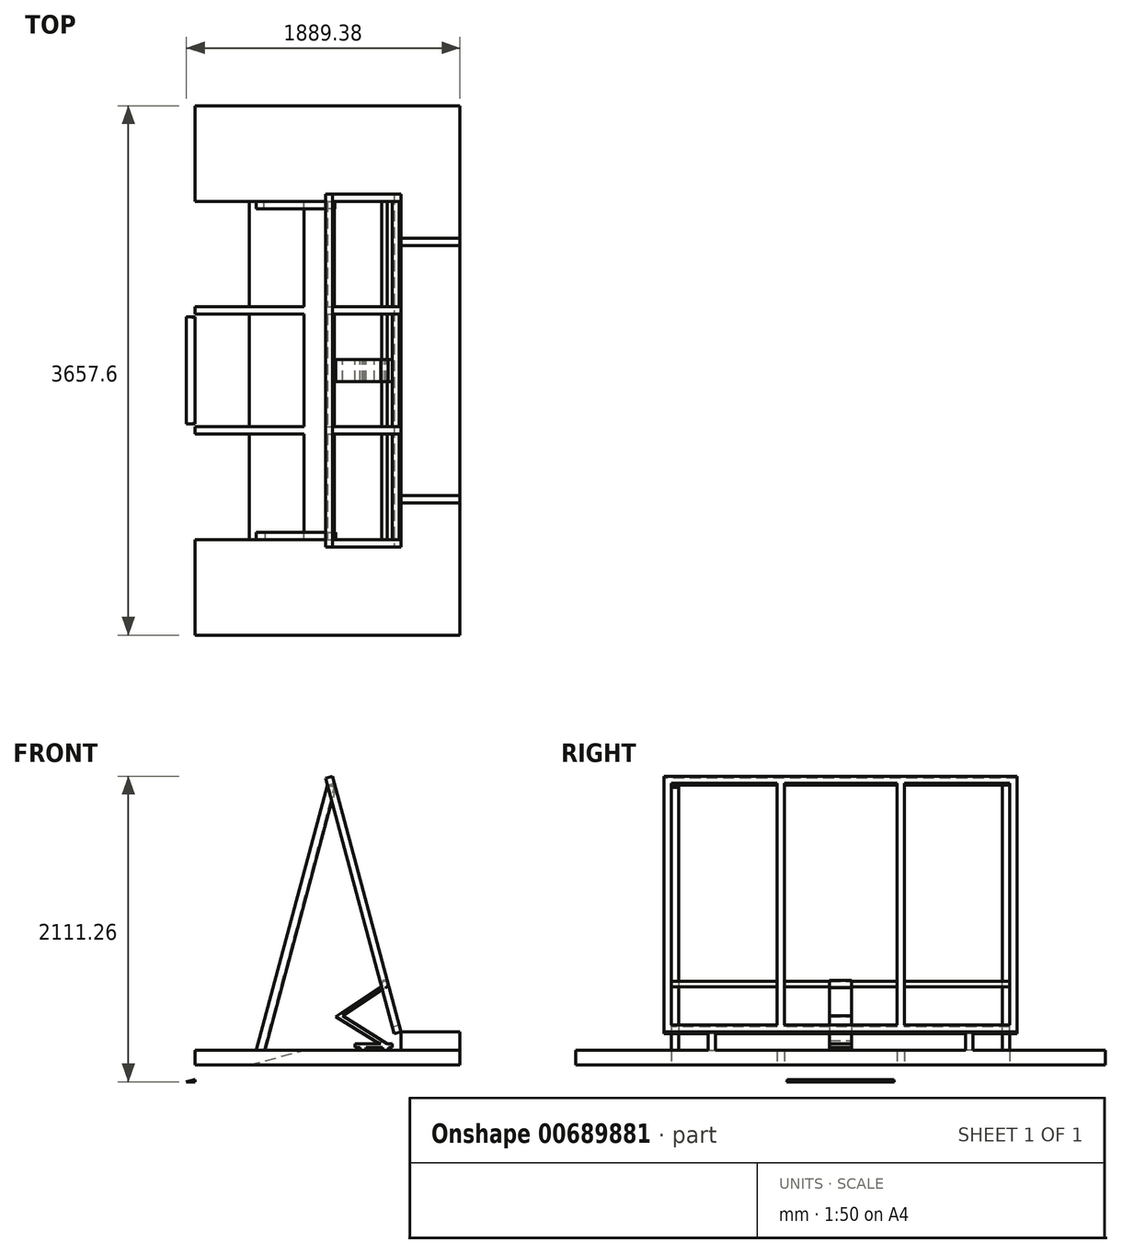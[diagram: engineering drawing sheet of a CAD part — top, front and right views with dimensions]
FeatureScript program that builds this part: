
annotation { "Feature Type Name" : "Feature", "Feature Type Description" : "" }
export const myFeature = defineFeature(function(context is Context, id is Id, definition is map)
    precondition{}
    {
        {
            var Q0;
            Q0=qCreatedBy(makeId("Top.planeOp"),FACE);
            var sketch = newSketch(context, id + "F0", { "sketchPlane" : qUnion([Q0])});
            skLineSegment(sketch, "E0.bottom", {"start": v(0, 0) * mm, "end": v(1828.8, 0) * mm});
            skLineSegment(sketch, "E0.top", {"start": v(0, 3657.6) * mm, "end": v(1828.8, 3657.6) * mm});
            skLineSegment(sketch, "E0.left", {"start": v(0, 0) * mm, "end": v(0, 3657.6) * mm});
            skLineSegment(sketch, "E0.right", {"start": v(1828.8, 0) * mm, "end": v(1828.8, 3657.6) * mm});
            skSolve(sketch);
        }
        {
            var Q0;
            Q0 = qSketchRegion(id + "F0", true);
            extrude(context, id + "F1", {"entities" : qUnion([Q0]), "oppositeDirection" : true, "depth" : 101.6 * mm, "offsetDistance" : 25.4 * mm});
        }
        {
            var Q0;
            Q0=qCreatedBy(makeId("Right.planeOp"),FACE);
            var sketch = newSketch(context, id + "F2", { "sketchPlane" : qUnion([Q0])});
            skArc(sketch, "E1", {"start": v(2199.73, -217.77) * mm, "mid": v(1828.8, 76.2) * mm, "end": v(1457.87, -217.77) * mm});
            skLineSegment(sketch, "E2", {"start": v(1457.87, -217.77) * mm, "end": v(2199.73, -217.77) * mm});
            skLineSegment(sketch, "E3", {"start": v(1657.07, 76.2) * mm, "end": v(2046.06, 76.2) * mm, "construction": true});
            skPoint(sketch, "E3.startSnap0", {"position": v(1828.8, 76.2) * mm});
            skSolve(sketch);
        }
        {
            var Q0;
            Q0 = qSketchRegion(id + "F2", true);
            extrude(context, id + "F3", {"entities" : qUnion([Q0]), "operationType" : NewBodyOperationType.ADD, "oppositeDirection" : true, "depth" : 304.8 * mm, "offsetDistance" : 25.4 * mm});
        }
        {
            var Q0;
            {var subQ0=sQuery(id+"F0.wireOp",EDGE,"E0.left");var subQ1=sQuery(id+"F2.wireOp",EDGE,"E1");Q0=makeQuery(id+"F3.boolean.opBoolean","SPLIT",FACE,{"disambiguationData":[TD([makeQuery(id+"F1.opExtrude","CAP_FACE",FACE,{"disambiguationData":[OSD([sQuery(id+"F0.wireOp",EDGE,"E0.bottom"),sQuery(id+"F0.wireOp",EDGE,"E0.top"),subQ0,sQuery(id+"F0.wireOp",EDGE,"E0.right")])],"isStart":true})])],"derivedFrom":makeQuery(id+"F3.opExtrude","CAP_FACE",FACE,{"disambiguationData":[OSD([subQ1,sQuery(id+"F2.wireOp",EDGE,"E2")])],"isStart":true})});}
            cPlane(context, id + "F4", {"entities" : qUnion([Q0]), "cplaneType" : CPlaneType.OFFSET, "offset" : 914.4 * mm, "width" : 152.4 * mm, "height" : 152.4 * mm});
        }
        {
            var Q0;
            Q0=makeQuery(id+"F1.opExtrude","CAP_FACE",FACE,{"disambiguationData":[OSD([sQuery(id+"F0.wireOp",EDGE,"E0.bottom"),sQuery(id+"F0.wireOp",EDGE,"E0.top"),sQuery(id+"F0.wireOp",EDGE,"E0.left"),sQuery(id+"F0.wireOp",EDGE,"E0.right")])],"isStart":true});
            var sketch = newSketch(context, id + "F5", { "sketchPlane" : qUnion([Q0])});
            skLineSegment(sketch, "E4", {"start": v(0, 1828.8) * mm, "end": v(1828.8, 1828.8) * mm, "construction": true});
            skLineSegment(sketch, "E5.bottom", {"start": v(1828.8, 914.4) * mm, "end": v(1422.4, 914.4) * mm});
            skLineSegment(sketch, "E5.top", {"start": v(1828.8, 965.2) * mm, "end": v(1422.4, 965.2) * mm});
            skLineSegment(sketch, "E5.left", {"start": v(1828.8, 914.4) * mm, "end": v(1828.8, 965.2) * mm});
            skLineSegment(sketch, "E5.right", {"start": v(1422.4, 914.4) * mm, "end": v(1422.4, 965.2) * mm});
            skLineSegment(sketch, "E6.MirrorCS", {"start": v(1828.8, 2743.2) * mm, "end": v(1422.4, 2743.2) * mm});
            skLineSegment(sketch, "E7.MirrorCS", {"start": v(1828.8, 2692.4) * mm, "end": v(1422.4, 2692.4) * mm});
            skLineSegment(sketch, "E8.MirrorCS", {"start": v(1422.4, 2743.2) * mm, "end": v(1422.4, 2692.4) * mm});
            skLineSegment(sketch, "E9.MirrorCS", {"start": v(1828.8, 2743.2) * mm, "end": v(1828.8, 2692.4) * mm});
            skSolve(sketch);
        }
        {
            var Q0;
            Q0 = qSketchRegion(id + "F5", true);
            extrude(context, id + "F6", {"entities" : qUnion([Q0]), "operationType" : NewBodyOperationType.ADD, "depth" : 127 * mm, "offsetDistance" : 25.4 * mm});
        }
        {
            var Q0;
            Q0=makeQuery(id+"F6.opExtrude","SWEPT_FACE",FACE,{"disambiguationData":[OSD([sQuery(id+"F5.wireOp",EDGE,"E5.bottom")])]});
            var sketch = newSketch(context, id + "F7", { "sketchPlane" : qUnion([Q0])});
            skLineSegment(sketch, "E10", {"start": v(1422.4, 127) * mm, "end": v(949.07, 1893.49) * mm});
            skLineSegment(sketch, "E11", {"start": v(949.07, 1893.49) * mm, "end": v(900, 1880.34) * mm});
            skLineSegment(sketch, "E12", {"start": v(900, 1880.34) * mm, "end": v(1373.33, 113.85) * mm});
            skLineSegment(sketch, "E13", {"start": v(1373.33, 113.85) * mm, "end": v(1422.4, 127) * mm});
            skSolve(sketch);
        }
        {
            var Q0;
            Q0 = qSketchRegion(id + "F7", true);
            extrude(context, id + "F8", {"entities" : qUnion([Q0]), "oppositeDirection" : true, "depth" : 2133.6 * mm, "offsetDistance" : 25.4 * mm});
        }
        {
            var Q0;
            Q0 = qSketchRegion(id + "F7", true);
            extrude(context, id + "F9", {"entities" : qUnion([Q0]), "operationType" : NewBodyOperationType.ADD, "depth" : 304.8 * mm, "offsetDistance" : 25.4 * mm});
        }
        {
            var Q0;
            {var subQ0=sQuery(id+"F7.wireOp",EDGE,"E10");Q0=makeQuery(id+"F9.boolean.opBoolean","MERGE",FACE,{"derivedFrom":[makeQuery(id+"F8.opExtrude","SWEPT_FACE",FACE,{"disambiguationData":[OSD([subQ0])]}),makeQuery(id+"F9.opExtrude","SWEPT_FACE",FACE,{"disambiguationData":[OSD([subQ0])]})]});}
            var sketch = newSketch(context, id + "F10", { "sketchPlane" : qUnion([Q0])});
            skLineSegment(sketch, "E14.bottom", {"start": v(660.4, 1532.53) * mm, "end": v(1388.52, 1532.53) * mm});
            skLineSegment(sketch, "E14.top", {"start": v(660.4, -194.67) * mm, "end": v(1388.52, -194.67) * mm});
            skLineSegment(sketch, "E14.left", {"start": v(660.4, 1532.53) * mm, "end": v(660.4, -194.67) * mm});
            skLineSegment(sketch, "E14.right", {"start": v(2997.2, 1532.53) * mm, "end": v(2997.2, -194.67) * mm});
            skLineSegment(sketch, "E15.left", {"start": v(1388.52, 1532.53) * mm, "end": v(1388.52, -194.67) * mm});
            skLineSegment(sketch, "E15.right", {"start": v(1439.32, 1532.53) * mm, "end": v(1439.32, -194.67) * mm});
            skLineSegment(sketch, "E16.left", {"start": v(2218.28, 1532.53) * mm, "end": v(2218.28, -194.67) * mm});
            skLineSegment(sketch, "E16.right", {"start": v(2269.08, 1532.53) * mm, "end": v(2269.08, -194.67) * mm});
            skLineSegment(sketch, "E17.trimOffspring", {"start": v(1439.32, 1532.53) * mm, "end": v(2218.28, 1532.53) * mm});
            skLineSegment(sketch, "E18.trimOffspring", {"start": v(1439.32, -194.67) * mm, "end": v(2218.28, -194.67) * mm});
            skLineSegment(sketch, "E19.trimOffspring", {"start": v(2269.08, -194.67) * mm, "end": v(2997.2, -194.67) * mm});
            skLineSegment(sketch, "E20.trimOffspring", {"start": v(2269.08, 1532.53) * mm, "end": v(2997.2, 1532.53) * mm});
            skSolve(sketch);
        }
        {
            var Q0;
            Q0 = qSketchRegion(id + "F10", true);
            extrude(context, id + "F11", {"entities" : qUnion([Q0]), "operationType" : NewBodyOperationType.REMOVE, "endBound" : BoundingType.THROUGH_ALL, "oppositeDirection" : true, "depth" : 25.4 * mm, "offsetDistance" : 25.4 * mm});
        }
        {
            var Q0;
            Q0=makeQuery(id+"F9.opExtrude","CAP_FACE",FACE,{"disambiguationData":[OSD([sQuery(id+"F7.wireOp",EDGE,"E10"),sQuery(id+"F7.wireOp",EDGE,"E11"),sQuery(id+"F7.wireOp",EDGE,"E12"),sQuery(id+"F7.wireOp",EDGE,"E13")])],"isStart":false});
            var sketch = newSketch(context, id + "F12", { "sketchPlane" : qUnion([Q0])});
            skLineSegment(sketch, "E21", {"start": v(1281.33, 457.2) * mm, "end": v(1281.33, 0) * mm, "construction": true});
            skLineSegment(sketch, "E22", {"start": v(1281.33, 457.2) * mm, "end": v(1333.92, 457.2) * mm, "construction": true});
            skCircle(sketch, "E23", {"center": v(1307.63, 457.2) * mm, "radius": 19.05 * mm});
            skSolve(sketch);
        }
        {
            var Q0;
            Q0 = qSketchRegion(id + "F12", true);
            extrude(context, id + "F13", {"entities" : qUnion([Q0]), "operationType" : NewBodyOperationType.ADD, "oppositeDirection" : true, "depth" : 2438.4 * mm, "offsetDistance" : 25.4 * mm});
        }
        {
            var Q0;
            Q0=qCreatedBy(makeId("Front.planeOp"),FACE);
            cPlane(context, id + "F14", {"entities" : qUnion([Q0]), "cplaneType" : CPlaneType.OFFSET, "offset" : 1828.8 * mm, "oppositeDirection" : true, "width" : 152.4 * mm, "height" : 152.4 * mm});
        }
        {
            var Q0;
            Q0=qCreatedBy(id+"F14.planeOp",FACE);
            var sketch = newSketch(context, id + "F15", { "sketchPlane" : qUnion([Q0])});
            skLineSegment(sketch, "E24", {"start": v(1281.33, 0) * mm, "end": v(1281.33, 457.2) * mm, "construction": true});
            skLineSegment(sketch, "E25", {"start": v(1281.33, 457.2) * mm, "end": v(1333.92, 457.2) * mm, "construction": true});
            skArc(sketch, "E26", {"start": v(1314.05, 432.63) * mm, "mid": v(1315.8, 481.25) * mm, "end": v(1287.57, 441.61) * mm});
            skLineSegment(sketch, "E27", {"start": v(1314.05, 432.63) * mm, "end": v(1018.16, 237.7) * mm});
            skLineSegment(sketch, "E28", {"start": v(1018.16, 237.7) * mm, "end": v(1327.7, 45.29) * mm});
            skLineSegment(sketch, "E29", {"start": v(1287.57, 441.61) * mm, "end": v(969.27, 231.92) * mm});
            skLineSegment(sketch, "E30", {"start": v(969.27, 231.92) * mm, "end": v(1237.34, 65.28) * mm});
            skLineSegment(sketch, "E31.bottom", {"start": v(1361.02, 45.29) * mm, "end": v(1327.7, 45.29) * mm});
            skLineSegment(sketch, "E31.top", {"start": v(1361.02, 20.35) * mm, "end": v(1336.7, 20.35) * mm});
            skLineSegment(sketch, "E31.left", {"start": v(1361.02, 45.29) * mm, "end": v(1361.02, 20.35) * mm});
            skLineSegment(sketch, "E31.right", {"start": v(1103.35, 45.29) * mm, "end": v(1103.35, 20.35) * mm});
            skArc(sketch, "E32", {"start": v(1138.95, 20.35) * mm, "mid": v(1160.24, -0.95) * mm, "end": v(1181.54, 20.35) * mm});
            skArc(sketch, "E33", {"start": v(1294.27, 20.35) * mm, "mid": v(1315.49, -0.88) * mm, "end": v(1336.7, 20.35) * mm});
            skLineSegment(sketch, "E34", {"start": v(1237.34, 65.28) * mm, "end": v(1281.33, 45.29) * mm});
            skLineSegment(sketch, "E35.trimOffspring", {"start": v(1281.33, 45.29) * mm, "end": v(1103.35, 45.29) * mm});
            skLineSegment(sketch, "E36.trimOffspring", {"start": v(1138.95, 20.35) * mm, "end": v(1103.35, 20.35) * mm});
            skLineSegment(sketch, "E37.trimOffspring", {"start": v(1294.27, 20.35) * mm, "end": v(1181.54, 20.35) * mm});
            skCircle(sketch, "E38", {"center": v(1307.63, 457.2) * mm, "radius": 19.18 * mm});
            skSolve(sketch);
        }
        {
            var Q0;
            Q0 = qSketchRegion(id + "F15", true);
            extrude(context, id + "F16", {"entities" : qUnion([Q0]), "operationType" : NewBodyOperationType.ADD, "depth" : 152.4 * mm, "offsetDistance" : 25.4 * mm, "symmetric" : true});
        }
        {
            var Q0;
            Q0=makeQuery(id+"F11.boolean.opBoolean","COPY",FACE,{"derivedFrom":makeQuery(id+"F11.opExtrude","SWEPT_FACE",FACE,{"disambiguationData":[OSD([sQuery(id+"F10.wireOp",EDGE,"E14.left")])]})});
            var sketch = newSketch(context, id + "F17", { "sketchPlane" : qUnion([Q0])});
            skLineSegment(sketch, "E39", {"start": v(-913.15, 1831.27) * mm, "end": v(-422.46, 0) * mm});
            skLineSegment(sketch, "E40", {"start": v(-913.15, 1831.27) * mm, "end": v(-969.81, 1816.09) * mm});
            skLineSegment(sketch, "E41", {"start": v(-969.81, 1816.09) * mm, "end": v(-483.2, 0) * mm});
            skLineSegment(sketch, "E42", {"start": v(-483.2, 0) * mm, "end": v(-422.46, 0) * mm});
            skSolve(sketch);
        }
        {
            var Q0;
            Q0 = qSketchRegion(id + "F17", true);
            extrude(context, id + "F18", {"entities" : qUnion([Q0]), "depth" : 50.8 * mm, "offsetDistance" : 25.4 * mm});
        }
        {
            var Q0;
            Q0=makeQuery(id+"F11.boolean.opBoolean","COPY",FACE,{"derivedFrom":makeQuery(id+"F11.opExtrude","SWEPT_FACE",FACE,{"disambiguationData":[OSD([sQuery(id+"F10.wireOp",EDGE,"E14.right")])]})});
            var sketch = newSketch(context, id + "F19", { "sketchPlane" : qUnion([Q0])});
            skLineSegment(sketch, "E43", {"start": v(913.15, 1831.27) * mm, "end": v(422.46, 0) * mm});
            skLineSegment(sketch, "E44", {"start": v(422.46, 0) * mm, "end": v(475.06, 0) * mm});
            skLineSegment(sketch, "E45", {"start": v(475.06, 0) * mm, "end": v(965.74, 1831.27) * mm});
            skLineSegment(sketch, "E46", {"start": v(965.74, 1831.27) * mm, "end": v(913.15, 1831.27) * mm});
            skSolve(sketch);
        }
        {
            var Q0;
            Q0 = qSketchRegion(id + "F19", true);
            extrude(context, id + "F20", {"entities" : qUnion([Q0]), "depth" : 50.8 * mm, "offsetDistance" : 25.4 * mm});
        }
    });
